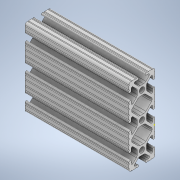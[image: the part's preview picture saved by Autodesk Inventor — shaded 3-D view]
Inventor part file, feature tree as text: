
AUTODESK INVENTOR PART (.ipt)
format: ipt  version: 2020 (Build 240168000, 168)  size: 368,640 bytes
history: native  units: in
note: dims shown in document units (in); Inventor stores cm internally (conversion verified against a paired STEP export)
features: sketch x2, extrude x1
ambient origin geometry x8: Origin, YZ Plane, XZ Plane, XY Plane, X Axis, Y Axis, Z Axis, Center Point
bodies: Solid1 (feature_tree)
feature tree (3):
  extrude  "Extrusion1"  [1 undecoded]
  sketch  "Sketch2"
  sketch  "Sketch1"  dims[d0=4.0in d1=0.0in]
note: 1 required parameter value undecoded (feature->parameter linkage not recoverable at this tier; creation-order binding heuristic only, values carry confidence <= 0.55)
